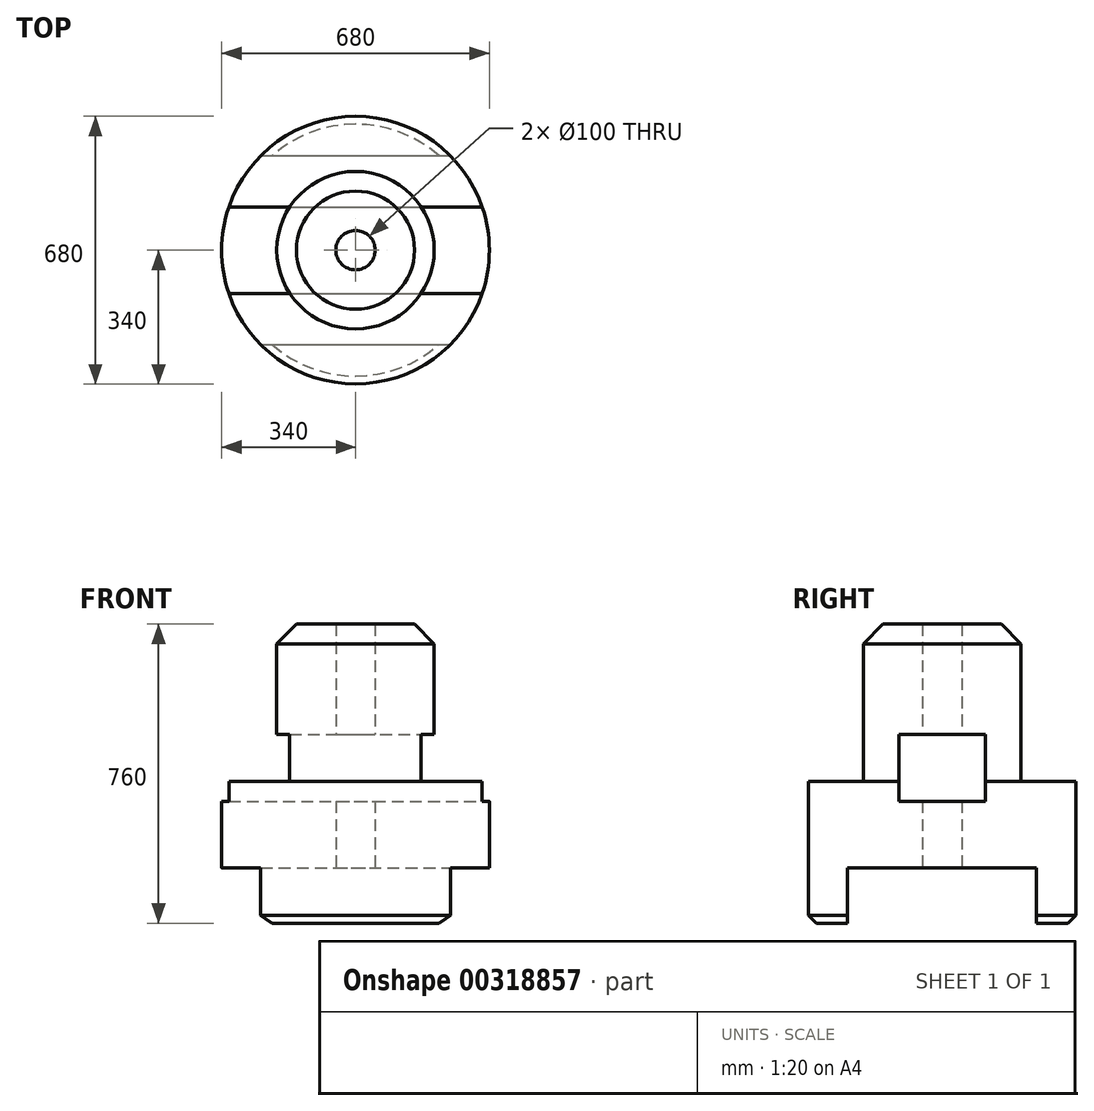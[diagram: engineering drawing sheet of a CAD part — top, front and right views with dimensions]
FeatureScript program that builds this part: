
annotation { "Feature Type Name" : "Feature", "Feature Type Description" : "" }
export const myFeature = defineFeature(function(context is Context, id is Id, definition is map)
    precondition{}
    {
        {
            var Q0;
            Q0=qCreatedBy(makeId("Front.planeOp"),FACE);
            var sketch = newSketch(context, id + "F0", { "sketchPlane" : qUnion([Q0])});
            skLineSegment(sketch, "E0", {"start": v(0, 760) * mm, "end": v(-200, 760) * mm});
            skLineSegment(sketch, "E1", {"start": v(-200, 760) * mm, "end": v(-200, 360) * mm});
            skLineSegment(sketch, "E2", {"start": v(-200, 360) * mm, "end": v(-340, 360) * mm});
            skLineSegment(sketch, "E3", {"start": v(-340, 360) * mm, "end": v(-340, 0) * mm});
            skLineSegment(sketch, "E4", {"start": v(-340, 0) * mm, "end": v(0, 0) * mm});
            skLineSegment(sketch, "E5", {"start": v(0, 0) * mm, "end": v(0, 760) * mm});
            skSolve(sketch);
        }
        {
            var Q0;
            Q0 = qSketchRegion(id + "F0", true);
            var Q1;
            Q1=sQuery(id+"F0.wireOp",EDGE,"E5");
            revolve(context, id + "F1", {"entities" : qUnion([Q0]), "axis" : qUnion([Q1]), "revolveType" : RevolveType.FULL});
        }
        {
            var Q0;
            Q0=makeQuery(id+"F1.opRevolve","SWEPT_EDGE",EDGE,{"disambiguationData":[OSD([sQuery(id+"F0.wireOp",EDGE,"E3"),sQuery(id+"F0.wireOp",EDGE,"E4")])]});
            chamfer(context, id + "F2", {"entities" : qUnion([Q0]), "width" : 20 * mm, "tangentPropagation" : true});
        }
        {
            var Q0;
            Q0=makeQuery(id+"F1.opRevolve","SWEPT_EDGE",EDGE,{"disambiguationData":[OSD([sQuery(id+"F0.wireOp",EDGE,"E0"),sQuery(id+"F0.wireOp",EDGE,"E1")])]});
            chamfer(context, id + "F3", {"entities" : qUnion([Q0]), "width" : 50 * mm, "tangentPropagation" : true});
        }
        {
            var Q0;
            Q0=qCreatedBy(makeId("Right.planeOp"),FACE);
            var sketch = newSketch(context, id + "F4", { "sketchPlane" : qUnion([Q0])});
            skLineSegment(sketch, "E6.bottom", {"start": v(-240, 0) * mm, "end": v(240, 0) * mm});
            skLineSegment(sketch, "E6.top", {"start": v(-240, 140) * mm, "end": v(240, 140) * mm});
            skLineSegment(sketch, "E6.left", {"start": v(-240, 0) * mm, "end": v(-240, 140) * mm});
            skLineSegment(sketch, "E6.right", {"start": v(240, 0) * mm, "end": v(240, 140) * mm});
            skSolve(sketch);
        }
        {
            var Q0;
            Q0 = qSketchRegion(id + "F4", true);
            extrude(context, id + "F5", {"entities" : qUnion([Q0]), "operationType" : NewBodyOperationType.REMOVE, "endBound" : BoundingType.SYMMETRIC, "oppositeDirection" : true, "depth" : 680 * mm});
        }
        {
            var Q0;
            Q0=qCreatedBy(makeId("Right.planeOp"),FACE);
            var sketch = newSketch(context, id + "F6", { "sketchPlane" : qUnion([Q0])});
            skLineSegment(sketch, "E7.bottom", {"start": v(-110, 310) * mm, "end": v(110, 310) * mm});
            skLineSegment(sketch, "E7.top", {"start": v(-110, 480) * mm, "end": v(110, 480) * mm});
            skLineSegment(sketch, "E7.left", {"start": v(-110, 310) * mm, "end": v(-110, 480) * mm});
            skLineSegment(sketch, "E7.right", {"start": v(110, 310) * mm, "end": v(110, 480) * mm});
            skSolve(sketch);
        }
        {
            var Q0;
            Q0 = qSketchRegion(id + "F6", true);
            extrude(context, id + "F7", {"entities" : qUnion([Q0]), "operationType" : NewBodyOperationType.REMOVE, "endBound" : BoundingType.SYMMETRIC, "oppositeDirection" : true, "depth" : 680 * mm});
        }
        {
            var Q0;
            Q0=makeQuery(id+"F5.boolean.opBoolean","COPY",FACE,{"derivedFrom":makeQuery(id+"F5.opExtrude","SWEPT_FACE",FACE,{"disambiguationData":[OSD([sQuery(id+"F4.wireOp",EDGE,"E6.top")])]})});
            var sketch = newSketch(context, id + "F8", { "sketchPlane" : qUnion([Q0])});
            skPoint(sketch, "E8", {"position": v(0, 0) * mm});
            skSolve(sketch);
        }
        {
            var Q0;
            Q0=sQuery(id+"F8.wireOp",VERTEX,"E8");
            var Q1;
            Q1=makeQuery(id+"F1.opRevolve","SWEPT_BODY",BODY,{"disambiguationData":[OSD([sQuery(id+"F0.wireOp",EDGE,"E0"),sQuery(id+"F0.wireOp",EDGE,"E1"),sQuery(id+"F0.wireOp",EDGE,"E2"),sQuery(id+"F0.wireOp",EDGE,"E3"),sQuery(id+"F0.wireOp",EDGE,"E4"),sQuery(id+"F0.wireOp",EDGE,"E5")])]});
            hole(context, id + "F9", {"style" : HoleStyle.SIMPLE, "endStyle" : HoleEndStyle.THROUGH, "holeDiameter" : 100 * mm, "tappedDepth" : 12 * mm, "tapClearance" : 3, "startFromSketch" : true, "locations" : qUnion([Q0]), "scope" : qUnion([Q1])});
        }
    });
